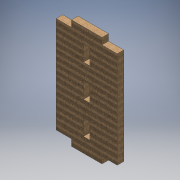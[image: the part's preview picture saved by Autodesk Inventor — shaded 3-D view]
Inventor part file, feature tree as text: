
AUTODESK INVENTOR PART (.ipt)
format: ipt  version: 2016 (Build 200138000, 138)  size: 168,960 bytes
history: native  units: mm
features: extrude x1, sketch x1
ambient origin geometry x8: Origin, YZ Plane, XZ Plane, XY Plane, X Axis, Y Axis, Z Axis, Center Point
bodies: Body1 (feature_tree)
feature tree (2):
  extrude  "Extrusion4"  Depth=14.945mm
  sketch  "Sketch1"  dims[d0=29.89mm d1=14.945mm d2=14.945mm d3=6.39mm d4=15.766857mm d6=6.3261mm d7=94.601145mm d15=7.883429mm d45=30.0mm d47=31.533715mm d48=10.0mm d50=10.0mm d52=6.39mm d53=0.0mm]
